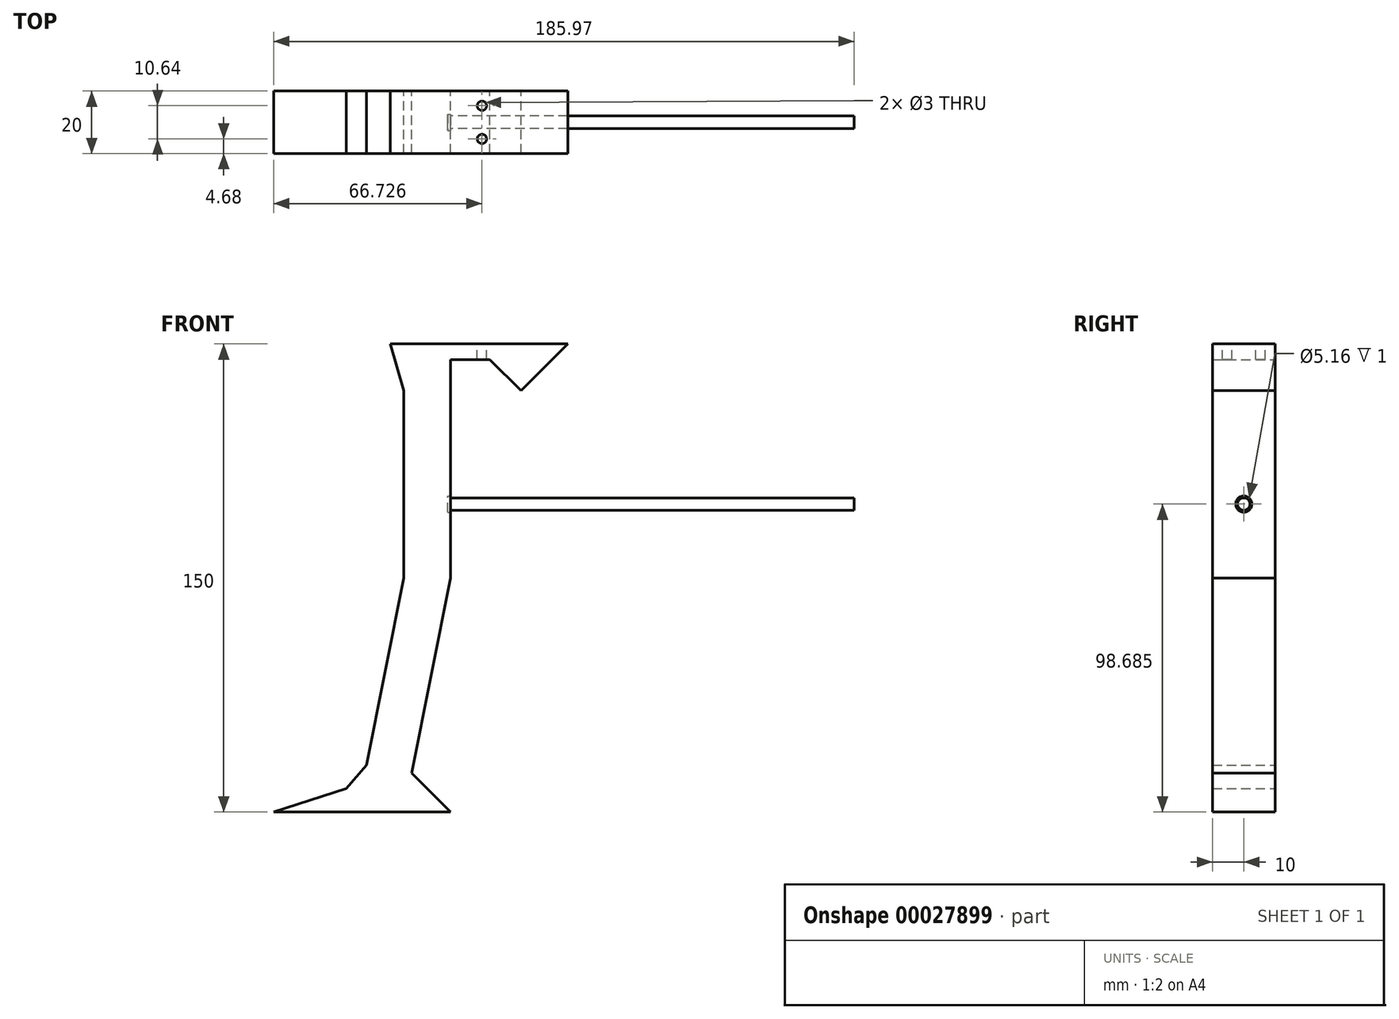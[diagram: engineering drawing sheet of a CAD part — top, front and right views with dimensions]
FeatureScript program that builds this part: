
annotation { "Feature Type Name" : "Feature", "Feature Type Description" : "" }
export const myFeature = defineFeature(function(context is Context, id is Id, definition is map)
    precondition{}
    {
        {
            var Q0;
            Q0=qCreatedBy(makeId("Front.planeOp"),FACE);
            var sketch = newSketch(context, id + "F0", { "sketchPlane" : qUnion([Q0])});
            skLineSegment(sketch, "E0.bottom", {"start": v(-46.95, 75) * mm, "end": v(28.05, 75) * mm});
            skLineSegment(sketch, "E0.top", {"start": v(-46.95, 0) * mm, "end": v(28.05, 0) * mm});
            skLineSegment(sketch, "E0.left", {"start": v(-46.95, 75) * mm, "end": v(-46.95, 0) * mm});
            skLineSegment(sketch, "E0.right", {"start": v(28.05, 75) * mm, "end": v(28.05, 0) * mm});
            skLineSegment(sketch, "E1", {"start": v(28.05, 60) * mm, "end": v(-31.95, 60) * mm});
            skLineSegment(sketch, "E2", {"start": v(-31.95, 60) * mm, "end": v(-31.95, 0) * mm});
            skLineSegment(sketch, "E3", {"start": v(-9.45, 75) * mm, "end": v(-9.45, 60) * mm});
            skLineSegment(sketch, "E4", {"start": v(-9.45, 60) * mm, "end": v(5.55, 75) * mm});
            skLineSegment(sketch, "E5", {"start": v(-46.95, 75) * mm, "end": v(-51.34, 75) * mm});
            skLineSegment(sketch, "E6", {"start": v(-51.34, 75) * mm, "end": v(-46.95, 60) * mm});
            skLineSegment(sketch, "E7", {"start": v(28.05, 0) * mm, "end": v(-46.95, -75) * mm});
            skLineSegment(sketch, "E8", {"start": v(-46.95, -75) * mm, "end": v(-61.95, -75) * mm});
            skLineSegment(sketch, "E9", {"start": v(-61.95, -75) * mm, "end": v(-46.95, 0) * mm});
            skLineSegment(sketch, "E10", {"start": v(-46.95, -75) * mm, "end": v(-31.95, 0) * mm});
            skLineSegment(sketch, "E11", {"start": v(-61.95, -75) * mm, "end": v(-71.95, -75) * mm});
            skLineSegment(sketch, "E12", {"start": v(-71.95, -75) * mm, "end": v(-58.95, -60) * mm});
            skLineSegment(sketch, "E13", {"start": v(-56.95, -75) * mm, "end": v(-43.95, -60) * mm});
            skLineSegment(sketch, "E14", {"start": v(-31.95, 19.68) * mm, "end": v(-31.95, 24.68) * mm});
            skLineSegment(sketch, "E15", {"start": v(-31.95, 60) * mm, "end": v(-31.95, 70) * mm});
            skLineSegment(sketch, "E16", {"start": v(-31.95, 70) * mm, "end": v(-9.45, 70) * mm});
            skPoint(sketch, "E16.endSnap0", {"position": v(-9.45, 67.5) * mm});
            skLineSegment(sketch, "E17", {"start": v(-19.45, 70) * mm, "end": v(-9.45, 60) * mm});
            skLineSegment(sketch, "E18", {"start": v(-65.45, -67.5) * mm, "end": v(-88.68, -75) * mm});
            skLineSegment(sketch, "E19", {"start": v(-88.68, -75) * mm, "end": v(-71.95, -75) * mm});
            skLineSegment(sketch, "E20", {"start": v(-46.95, -75) * mm, "end": v(-31.95, -75) * mm});
            skLineSegment(sketch, "E21", {"start": v(-31.95, -75) * mm, "end": v(-39.45, -67.5) * mm});
            skLineSegment(sketch, "E22", {"start": v(-39.45, -67.5) * mm, "end": v(-44.45, -62.5) * mm});
            skSolve(sketch);
        }
        {
            var Q0;
            {var subQ1=sQuery(id+"F0.wireOp",EDGE,"cec4a44a-0353-401e-a1ed-aaa4011a612b");Q0=makeQuery(id+"F0.imprint","IMPRINT",FACE,{"disambiguationData":[TD([[makeQuery(id+"F0.imprint","IMPRINT",EDGE,{"derivedFrom":subQ1}),1.0]])]});}
            var Q1;
            {var subQ3=sQuery(id+"F0.wireOp",EDGE,"E0.left");Q1=makeQuery(id+"F0.imprint","IMPRINT",FACE,{"disambiguationData":[TD([[makeQuery(id+"F0.imprint","IMPRINT",EDGE,{"derivedFrom":subQ3}),1.0]])]});}
            var Q2;
            {var subQ1=sQuery(id+"F0.wireOp",EDGE,"E3");Q2=makeQuery(id+"F0.imprint","IMPRINT",FACE,{"disambiguationData":[TD([[makeQuery(id+"F0.imprint","IMPRINT",EDGE,{"derivedFrom":subQ1}),1.0]])]});}
            var Q3;
            {var subQ1=sQuery(id+"F0.wireOp",EDGE,"E5");Q3=makeQuery(id+"F0.imprint","IMPRINT",FACE,{"disambiguationData":[TD([[makeQuery(id+"F0.imprint","IMPRINT",EDGE,{"derivedFrom":subQ1}),1.0]])]});}
            var Q4;
            {var subQ1=sQuery(id+"F0.wireOp",EDGE,"E13");Q4=makeQuery(id+"F0.imprint","IMPRINT",FACE,{"disambiguationData":[TD([[makeQuery(id+"F0.imprint","IMPRINT",EDGE,{"derivedFrom":subQ1}),1.0]])]});}
            var Q5;
            {var subQ1=sQuery(id+"F0.wireOp",EDGE,"E11");Q5=makeQuery(id+"F0.imprint","IMPRINT",FACE,{"disambiguationData":[TD([[makeQuery(id+"F0.imprint","IMPRINT",EDGE,{"derivedFrom":subQ1}),-1.0]])]});}
            var Q6;
            {var subQ0=sQuery(id+"F0.wireOp",EDGE,"E17");Q6=makeQuery(id+"F0.imprint","IMPRINT",FACE,{"disambiguationData":[TD([[makeQuery(id+"F0.imprint","IMPRINT",EDGE,{"derivedFrom":subQ0}),1.0]])]});}
            var Q7;
            {var subQ0=sQuery(id+"F0.wireOp",EDGE,"0af0b818-f1c4-4242-8e4c-e54c71e078cd");Q7=makeQuery(id+"F0.imprint","IMPRINT",FACE,{"disambiguationData":[TD([[makeQuery(id+"F0.imprint","IMPRINT",EDGE,{"derivedFrom":subQ0}),-1.0]])]});}
            var Q8;
            {var subQ0=sQuery(id+"F0.wireOp",EDGE,"E13");Q8=makeQuery(id+"F0.imprint","IMPRINT",FACE,{"disambiguationData":[TD([[makeQuery(id+"F0.imprint","IMPRINT",EDGE,{"derivedFrom":subQ0}),-1.0]])]});}
            var Q9;
            {var subQ0=sQuery(id+"F0.wireOp",EDGE,"E22");Q9=makeQuery(id+"F0.imprint","IMPRINT",FACE,{"disambiguationData":[TD([[makeQuery(id+"F0.imprint","IMPRINT",EDGE,{"derivedFrom":subQ0}),1.0]])]});}
            var Q10;
            {var subQ1=sQuery(id+"F0.wireOp",EDGE,"E20");Q10=makeQuery(id+"F0.imprint","IMPRINT",FACE,{"disambiguationData":[TD([[makeQuery(id+"F0.imprint","IMPRINT",EDGE,{"derivedFrom":subQ1}),1.0]])]});}
            var Q11;
            {var subQ1=sQuery(id+"F0.wireOp",EDGE,"E18");Q11=makeQuery(id+"F0.imprint","IMPRINT",FACE,{"disambiguationData":[TD([[makeQuery(id+"F0.imprint","IMPRINT",EDGE,{"derivedFrom":subQ1}),1.0]])]});}
            extrude(context, id + "F1", {"entities" : qUnion([Q0, Q1, Q2, Q3, Q4, Q5, Q6, Q7, Q8, Q9, Q10, Q11]), "depth" : 20 * mm});
        }
        {
            var Q0;
            Q0=makeQuery(id+"F1.opExtrude","SWEPT_FACE",FACE,{"disambiguationData":[OSD([sQuery(id+"F0.wireOp",EDGE,"E0.bottom")])]});
            var sketch = newSketch(context, id + "F2", { "sketchPlane" : qUnion([Q0])});
            skLineSegment(sketch, "E23", {"start": v(-51.34, -10) * mm, "end": v(5.55, -10) * mm, "construction": true});
            skCircle(sketch, "E24", {"center": v(-21.95, -15.32) * mm, "radius": 1.5 * mm});
            skCircle(sketch, "E25.MirrorC", {"center": v(-21.95, -4.68) * mm, "radius": 1.5 * mm});
            skSolve(sketch);
        }
        {
            var Q0;
            Q0 = qSketchRegion(id + "F2", true);
            extrude(context, id + "F3", {"entities" : qUnion([Q0]), "operationType" : NewBodyOperationType.REMOVE, "oppositeDirection" : true, "depth" : 20 * mm});
        }
        {
            var Q0;
            Q0=makeQuery(id+"F1.opExtrude","SWEPT_FACE",FACE,{"disambiguationData":[OSD([sQuery(id+"F0.wireOp",EDGE,"E2"),sQuery(id+"F0.wireOp",EDGE,"E14")])]});
            var sketch = newSketch(context, id + "F4", { "sketchPlane" : qUnion([Q0])});
            skLineSegment(sketch, "E26", {"start": v(-10, 47.37) * mm, "end": v(-10, 0) * mm, "construction": true});
            skCircle(sketch, "E27", {"center": v(-10, 23.68) * mm, "radius": 2 * mm});
            skSolve(sketch);
        }
        {
            var Q0;
            Q0=makeQuery(id+"F4.imprint","IMPRINT",FACE,{"disambiguationData":[TD([[makeQuery(id+"F4.imprint","IMPRINT",EDGE,{"derivedFrom":sQuery(id+"F4.wireOp",EDGE,"E27")}),1.0]])]});
            extrude(context, id + "F5", {"entities" : qUnion([Q0]), "operationType" : NewBodyOperationType.ADD, "depth" : 129.24 * mm, "hasSecondDirection" : true, "secondDirectionOppositeDirection" : true, "secondDirectionDepth" : 1 * mm});
        }
        {
            var Q0;
            Q0=makeQuery(id+"F1.opExtrude","SWEPT_FACE",FACE,{"disambiguationData":[OSD([sQuery(id+"F0.wireOp",EDGE,"E2"),sQuery(id+"F0.wireOp",EDGE,"E14")])]});
            var sketch = newSketch(context, id + "F6", { "sketchPlane" : qUnion([Q0])});
            skCircle(sketch, "E28", {"center": v(-10, 23.68) * mm, "radius": 2.58 * mm});
            skLineSegment(sketch, "E29", {"start": v(0, 32.7) * mm, "end": v(0, 17.66) * mm, "construction": true});
            skLineSegment(sketch, "E30", {"start": v(-20, 17.66) * mm, "end": v(-20, 32.7) * mm, "construction": true});
            skLineSegment(sketch, "E31", {"start": v(-20, 32.7) * mm, "end": v(-20, 17.66) * mm, "construction": true});
            skSolve(sketch);
        }
        {
            var Q0;
            Q0 = qSketchRegion(id + "F6", true);
            extrude(context, id + "F7", {"entities" : qUnion([Q0]), "operationType" : NewBodyOperationType.REMOVE, "oppositeDirection" : true, "depth" : 1 * mm});
        }
    });
